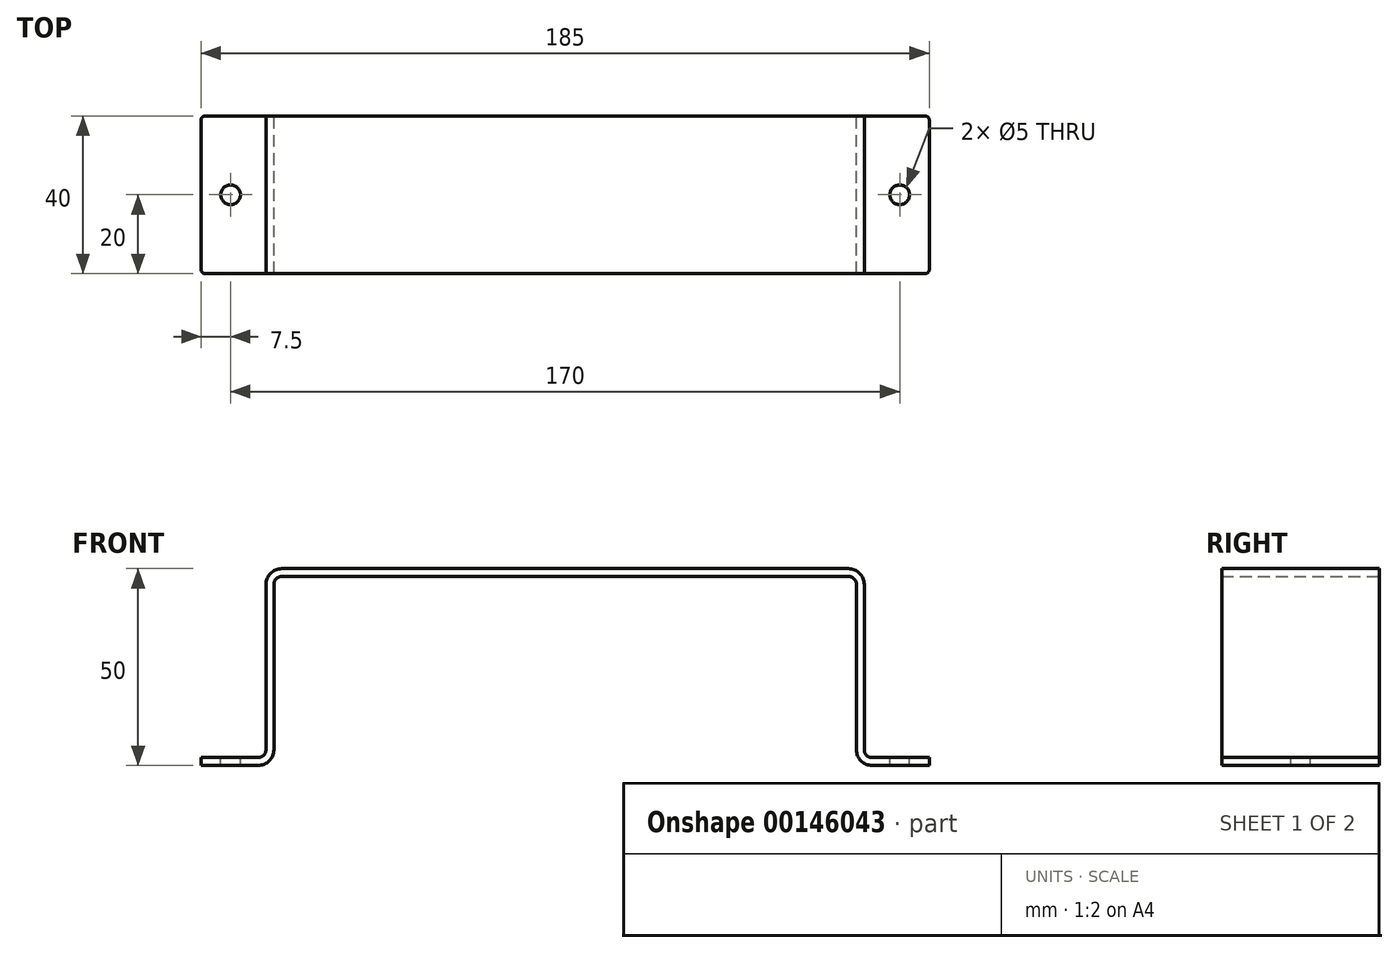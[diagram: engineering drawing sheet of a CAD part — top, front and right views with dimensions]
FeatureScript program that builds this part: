
annotation { "Feature Type Name" : "Feature", "Feature Type Description" : "" }
export const myFeature = defineFeature(function(context is Context, id is Id, definition is map)
    precondition{}
    {
        {
            var Q0;
            Q0=qCreatedBy(makeId("Front.planeOp"),FACE);
            var sketch = newSketch(context, id + "F0", { "sketchPlane" : qUnion([Q0])});
            skLineSegment(sketch, "E0", {"start": v(-92.5, 0) * mm, "end": v(-92.5, 2) * mm});
            skLineSegment(sketch, "E1", {"start": v(-92.5, 2) * mm, "end": v(-78, 2) * mm});
            skLineSegment(sketch, "E2", {"start": v(-76, 4) * mm, "end": v(-76, 46) * mm});
            skLineSegment(sketch, "E3", {"start": v(-72, 50) * mm, "end": v(0, 50) * mm});
            skLineSegment(sketch, "E4", {"start": v(0, 50) * mm, "end": v(0, 0) * mm, "construction": true});
            skLineSegment(sketch, "E5", {"start": v(-92.5, 0) * mm, "end": v(-78, 0) * mm});
            skLineSegment(sketch, "E6", {"start": v(-74, 4) * mm, "end": v(-74, 46) * mm});
            skLineSegment(sketch, "E7", {"start": v(-72, 48) * mm, "end": v(0, 48) * mm});
            skPoint(sketch, "E8.visualSharp", {"position": v(-76, 50) * mm});
            skArc(sketch, "E8.filletArc", {"start": v(-72, 50) * mm, "mid": v(-74.83, 48.83) * mm, "end": v(-76, 46) * mm});
            skPoint(sketch, "E9.visualSharp", {"position": v(-74, 0) * mm});
            skArc(sketch, "E9.filletArc", {"start": v(-78, 0) * mm, "mid": v(-75.17, 1.17) * mm, "end": v(-74, 4) * mm});
            skPoint(sketch, "E10.visualSharp", {"position": v(-74, 48) * mm});
            skArc(sketch, "E10.filletArc", {"start": v(-72, 48) * mm, "mid": v(-73.41, 47.41) * mm, "end": v(-74, 46) * mm});
            skPoint(sketch, "E11.visualSharp", {"position": v(-76, 2) * mm});
            skArc(sketch, "E11.filletArc", {"start": v(-78, 2) * mm, "mid": v(-76.59, 2.59) * mm, "end": v(-76, 4) * mm});
            skArc(sketch, "E12.MirrorCS", {"start": v(78, 2) * mm, "mid": v(76.59, 2.59) * mm, "end": v(76, 4) * mm});
            skArc(sketch, "E13.MirrorCS", {"start": v(72, 48) * mm, "mid": v(73.41, 47.41) * mm, "end": v(74, 46) * mm});
            skArc(sketch, "E14.MirrorCS", {"start": v(78, 0) * mm, "mid": v(75.17, 1.17) * mm, "end": v(74, 4) * mm});
            skLineSegment(sketch, "E15.MirrorCS", {"start": v(92.5, 0) * mm, "end": v(92.5, 2) * mm});
            skArc(sketch, "E16.MirrorCS", {"start": v(72, 50) * mm, "mid": v(74.83, 48.83) * mm, "end": v(76, 46) * mm});
            skPoint(sketch, "E17.MirrorP", {"position": v(76, 50) * mm});
            skPoint(sketch, "E18.MirrorP", {"position": v(74, 0) * mm});
            skPoint(sketch, "E19.MirrorP", {"position": v(74, 48) * mm});
            skPoint(sketch, "E20.MirrorP", {"position": v(76, 2) * mm});
            skLineSegment(sketch, "E21.MirrorCS", {"start": v(92.5, 2) * mm, "end": v(78, 2) * mm});
            skLineSegment(sketch, "E22.MirrorCS", {"start": v(76, 4) * mm, "end": v(76, 46) * mm});
            skLineSegment(sketch, "E23.MirrorCS", {"start": v(72, 48) * mm, "end": v(0, 48) * mm});
            skLineSegment(sketch, "E24.MirrorCS", {"start": v(74, 4) * mm, "end": v(74, 46) * mm});
            skLineSegment(sketch, "E25.MirrorCS", {"start": v(92.5, 0) * mm, "end": v(78, 0) * mm});
            skLineSegment(sketch, "E26.MirrorCS", {"start": v(72, 50) * mm, "end": v(0, 50) * mm});
            skSolve(sketch);
        }
        {
            var Q0;
            Q0=qSketchRegion(id+"F0",true);
            extrude(context, id + "F1", {"entities" : qUnion([Q0]), "endBound" : BoundingType.SYMMETRIC, "depth" : 40 * mm});
        }
        {
            var Q0;
            Q0=makeQuery(id+"F1.opExtrude","SWEPT_FACE",FACE,{"disambiguationData":[OSD([sQuery(id+"F0.wireOp",EDGE,"E1")])]});
            var sketch = newSketch(context, id + "F2", { "sketchPlane" : qUnion([Q0])});
            skCircle(sketch, "E27", {"center": v(-85, 0) * mm, "radius": 2.5 * mm});
            skPoint(sketch, "E27.centerSnap0", {"position": v(-92.5, 0) * mm});
            skCircle(sketch, "E28", {"center": v(85, 0) * mm, "radius": 2.5 * mm});
            skSolve(sketch);
        }
        {
            var Q0;
            Q0=qSketchRegion(id+"F2",true);
            extrude(context, id + "F3", {"entities" : qUnion([Q0]), "operationType" : NewBodyOperationType.REMOVE, "endBound" : BoundingType.THROUGH_ALL, "oppositeDirection" : true, "depth" : 25 * mm});
        }
        {
            var Q0;
            Q0=makeQuery(id+"F1.opExtrude","CAP_EDGE",EDGE,{"disambiguationData":[OSD([sQuery(id+"F0.wireOp",EDGE,"E0")])],"isStart":false});
            var Q1;
            Q1=makeQuery(id+"F1.opExtrude","CAP_EDGE",EDGE,{"disambiguationData":[OSD([sQuery(id+"F0.wireOp",EDGE,"E0")])],"isStart":true});
            var Q2;
            Q2=makeQuery(id+"F1.opExtrude","CAP_EDGE",EDGE,{"disambiguationData":[OSD([sQuery(id+"F0.wireOp",EDGE,"E15.MirrorCS")])],"isStart":false});
            var Q3;
            Q3=makeQuery(id+"F1.opExtrude","CAP_EDGE",EDGE,{"disambiguationData":[OSD([sQuery(id+"F0.wireOp",EDGE,"E15.MirrorCS")])],"isStart":true});
            fillet(context, id + "F4", {"entities" : qUnion([Q0, Q1, Q2, Q3]), "radius" : 1 * mm, "tangentPropagation" : true, "allowEdgeOverflow" : false});
        }
    });
